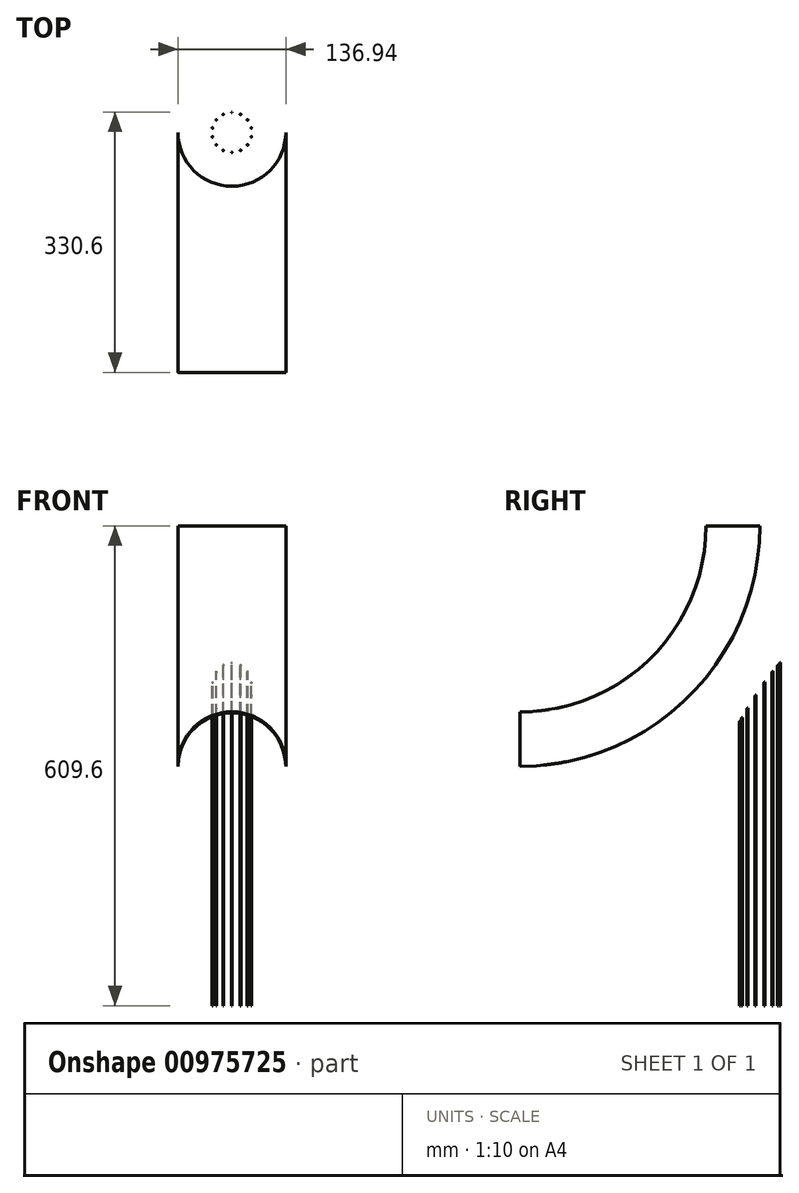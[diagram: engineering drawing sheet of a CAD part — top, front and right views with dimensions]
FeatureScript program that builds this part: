
annotation { "Feature Type Name" : "Feature", "Feature Type Description" : "" }
export const myFeature = defineFeature(function(context is Context, id is Id, definition is map)
    precondition{}
    {
        {
            var Q0;
            Q0=qCreatedBy(makeId("Right.planeOp"),FACE);
            var sketch = newSketch(context, id + "F0", { "sketchPlane" : qUnion([Q0])});
            skArc(sketch, "E0", {"start": v(-304.8, -304.8) * mm, "mid": v(-89.27, -215.53) * mm, "end": v(0, 0) * mm});
            skSolve(sketch);
        }
        {
            var Q0;
            Q0=qCreatedBy(makeId("Top.planeOp"),FACE);
            var sketch = newSketch(context, id + "F1", { "sketchPlane" : qUnion([Q0])});
            skCircle(sketch, "E1", {"center": v(0, 0) * mm, "radius": 68.47 * mm});
            skCircle(sketch, "E2", {"center": v(0, 0) * mm, "radius": 61.45 * mm});
            skSolve(sketch);
        }
        {
            var Q0;
            Q0 = qSketchRegion(id + "F0", true);
            var Q1;
            Q1 = qSketchRegion(id + "F1", true);
            var Q2;
            Q2=sQuery(id+"F0.wireOp",EDGE,"E0");
            sweep(context, id + "F2", {"profiles" : qUnion([Q0, Q1]), "path" : qUnion([Q2])});
        }
        {
            var Q0;
            Q0=qCreatedBy(makeId("Top.planeOp"),FACE);
            var sketch = newSketch(context, id + "F3", { "sketchPlane" : qUnion([Q0])});
            skLineSegment(sketch, "E3.bottom", {"start": v(-0.4, 25) * mm, "end": v(0.4, 25) * mm});
            skLineSegment(sketch, "E3.top", {"start": v(-0.4, 25.8) * mm, "end": v(0.4, 25.8) * mm});
            skLineSegment(sketch, "E3.left", {"start": v(-0.4, 25) * mm, "end": v(-0.4, 25.8) * mm});
            skLineSegment(sketch, "E3.right", {"start": v(0.4, 25) * mm, "end": v(0.4, 25.8) * mm});
            skPoint(sketch, "E3.middle", {"position": v(0, 25.4) * mm});
            skCircle(sketch, "E4", {"center": v(0, 0) * mm, "radius": 25.4 * mm, "construction": true});
            skSolve(sketch);
        }
        {
            var Q0;
            Q0 = qSketchRegion(id + "F3", true);
            extrude(context, id + "F4", {"entities" : qUnion([Q0]), "oppositeDirection" : true, "depth" : 609.6 * mm, "offsetDistance" : 25.4 * mm});
        }
        {
            var Q0;
            Q0=qCreatedBy(makeId("Front.planeOp"),FACE);
            var sketch = newSketch(context, id + "F5", { "sketchPlane" : qUnion([Q0])});
            skLineSegment(sketch, "E5", {"start": v(0, 0) * mm, "end": v(0, 50.22) * mm, "construction": true});
            skSolve(sketch);
        }
        {
            var Q0;
            Q0=makeQuery(id+"F4.opExtrude","SWEPT_BODY",BODY,{"disambiguationData":[OSD([sQuery(id+"F3.wireOp",EDGE,"E3.bottom"),sQuery(id+"F3.wireOp",EDGE,"E3.top"),sQuery(id+"F3.wireOp",EDGE,"E3.left"),sQuery(id+"F3.wireOp",EDGE,"E3.right")])]});
            var Q1;
            Q1=sQuery(id+"F5.wireOp",EDGE,"E5");
            circularPattern(context, id + "F6", {"entities" : qUnion([Q0]), "axis" : qUnion([Q1]), "angle" : 360 * degree, "instanceCount" : 14, "equalSpace" : true});
        }
        {
            var Q0;
            Q0=makeQuery(id+"F2.opSweep","CAP_FACE",FACE,{"disambiguationData":[OSD([sQuery(id+"F0.wireOp",VERTEX,"E0.end"),sQuery(id+"F1.wireOp",EDGE,"E1"),sQuery(id+"F1.wireOp",EDGE,"E2")])],"isStart":true});
            var sketch = newSketch(context, id + "F7", { "sketchPlane" : qUnion([Q0])});
            skCircle(sketch, "E6.0", {"center": v(0, 0) * mm, "radius": 68.47 * mm});
            skLineSegment(sketch, "E7", {"start": v(0, -306.2) * mm, "end": v(136.75, -306.2) * mm, "construction": true});
            skSolve(sketch);
        }
        {
            var Q0;
            Q0=qCreatedBy(makeId("Right.planeOp"),FACE);
            var sketch = newSketch(context, id + "F8", { "sketchPlane" : qUnion([Q0])});
            skArc(sketch, "E8.0", {"start": v(-304.8, -304.8) * mm, "mid": v(-89.27, -215.53) * mm, "end": v(0, 0) * mm});
            skSolve(sketch);
        }
        {
            var Q0;
            Q0 = qSketchRegion(id + "F7", true);
            var Q1;
            Q1 = qSketchRegion(id + "F8", true);
            var Q2;
            Q2=sQuery(id+"F7.wireOp",EDGE,"E7");
            revolve(context, id + "F9", {"operationType" : NewBodyOperationType.REMOVE, "surfaceOperationType" : NewSurfaceOperationType.NEW, "entities" : qUnion([Q0, Q1]), "axis" : qUnion([Q2]), "revolveType" : RevolveType.FULL, "oppositeDirection" : true});
        }
    });
